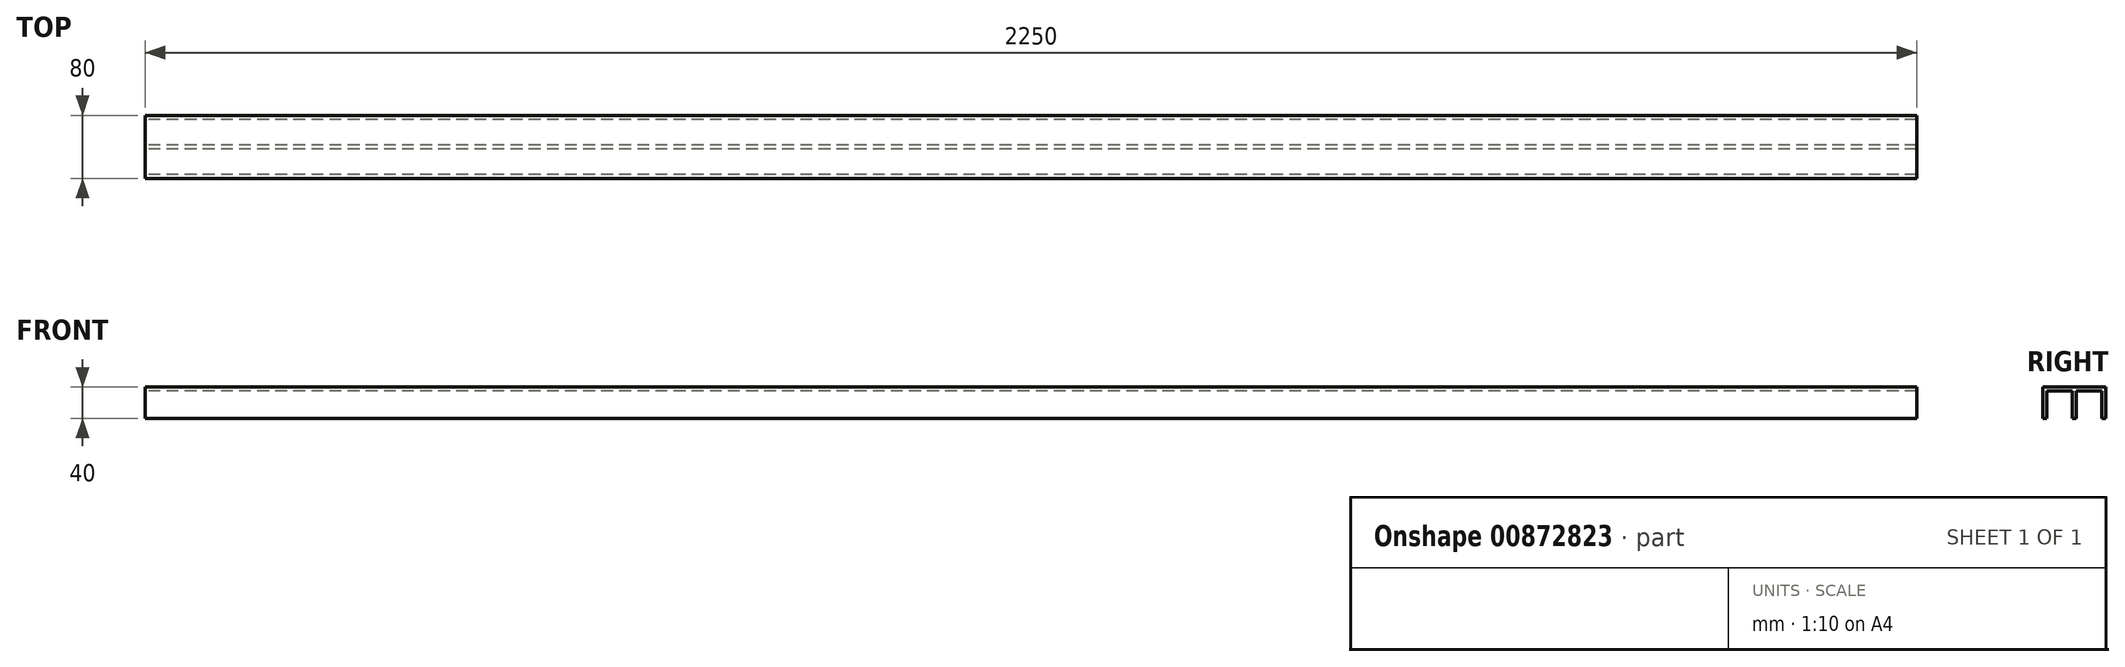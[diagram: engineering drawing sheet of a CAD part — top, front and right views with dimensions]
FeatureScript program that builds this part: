
annotation { "Feature Type Name" : "Feature", "Feature Type Description" : "" }
export const myFeature = defineFeature(function(context is Context, id is Id, definition is map)
    precondition{}
    {
        {
            var Q0;
            Q0=qCreatedBy(makeId("Right.planeOp"),FACE);
            var sketch = newSketch(context, id + "F0", { "sketchPlane" : qUnion([Q0])});
            skLineSegment(sketch, "E0", {"start": v(-47.13, 0) * mm, "end": v(-47.13, 40) * mm});
            skLineSegment(sketch, "E1", {"start": v(-47.13, 40) * mm, "end": v(32.87, 40) * mm});
            skLineSegment(sketch, "E2", {"start": v(32.87, 40) * mm, "end": v(32.87, 0) * mm});
            skLineSegment(sketch, "E3", {"start": v(32.87, 0) * mm, "end": v(27.87, 0) * mm});
            skLineSegment(sketch, "E4", {"start": v(27.87, 0) * mm, "end": v(27.87, 35) * mm});
            skLineSegment(sketch, "E5", {"start": v(27.87, 35) * mm, "end": v(-4.63, 35) * mm});
            skLineSegment(sketch, "E6", {"start": v(-4.63, 35) * mm, "end": v(-4.63, 0) * mm});
            skLineSegment(sketch, "E7", {"start": v(-4.63, 0) * mm, "end": v(-9.63, 0) * mm});
            skLineSegment(sketch, "E8", {"start": v(-9.63, 0) * mm, "end": v(-9.63, 35) * mm});
            skLineSegment(sketch, "E9", {"start": v(-9.63, 35) * mm, "end": v(-42.13, 35) * mm});
            skLineSegment(sketch, "E10", {"start": v(-42.13, 35) * mm, "end": v(-42.13, 0) * mm});
            skLineSegment(sketch, "E11", {"start": v(-42.13, 0) * mm, "end": v(-47.13, 0) * mm});
            skSolve(sketch);
        }
        {
            var Q0;
            Q0 = qSketchRegion(id + "F0", true);
            extrude(context, id + "F1", {"entities" : qUnion([Q0]), "depth" : 2250 * mm, "offsetDistance" : 25 * mm});
        }
    });
